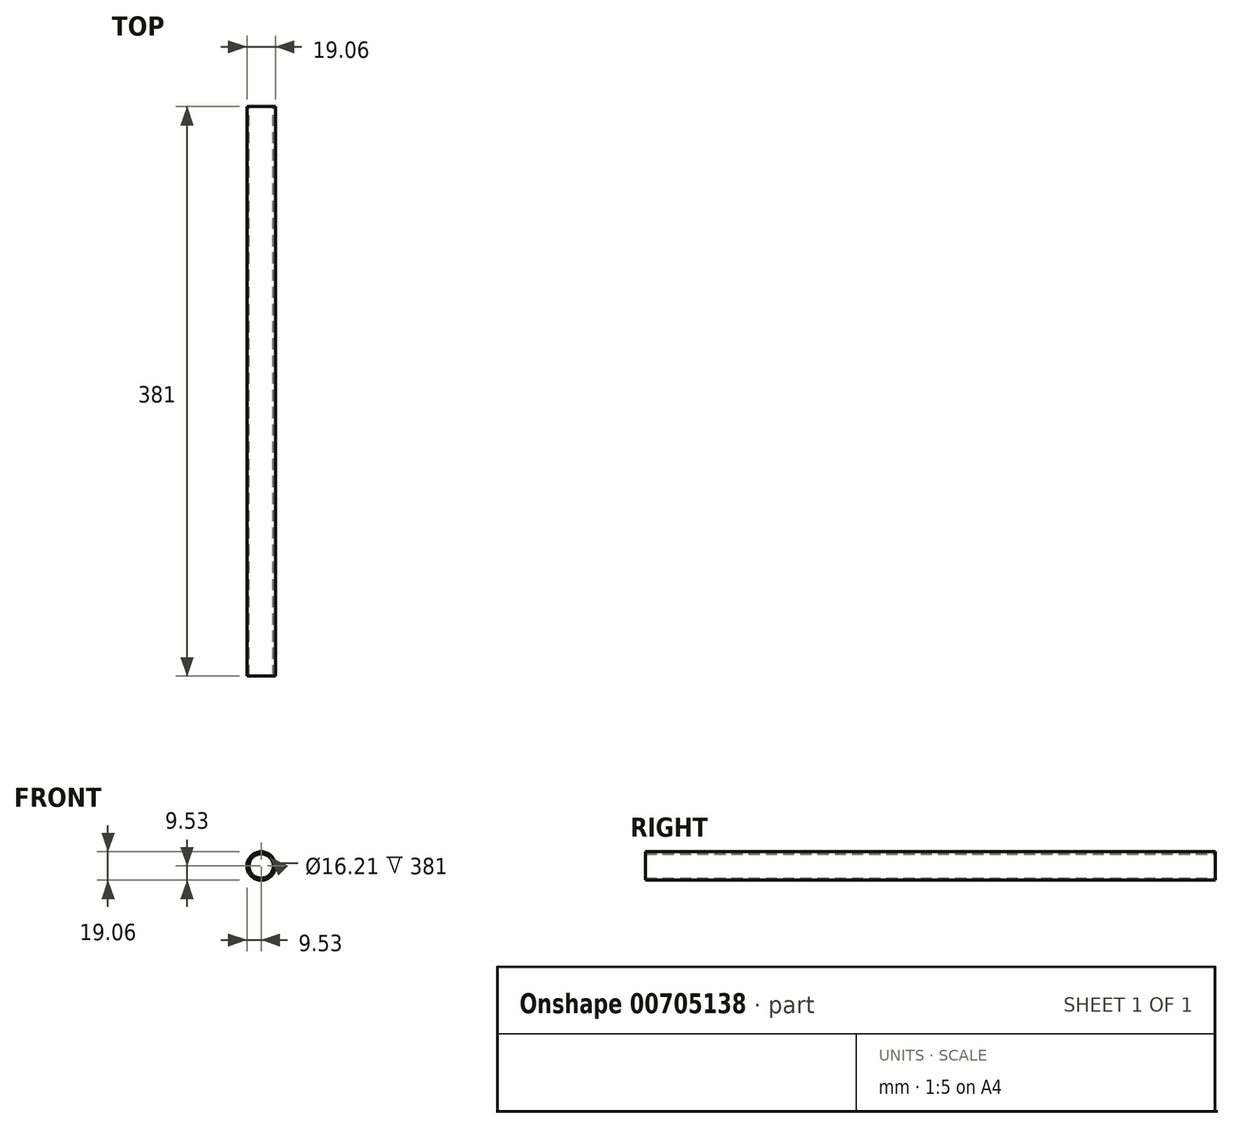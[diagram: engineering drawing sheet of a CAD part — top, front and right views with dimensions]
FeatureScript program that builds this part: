
annotation { "Feature Type Name" : "Feature", "Feature Type Description" : "" }
export const myFeature = defineFeature(function(context is Context, id is Id, definition is map)
    precondition{}
    {
        {
            var Q0;
            Q0=qCreatedBy(makeId("Front.planeOp"),FACE);
            var sketch = newSketch(context, id + "F0", { "sketchPlane" : qUnion([Q0])});
            skCircle(sketch, "E0", {"center": v(0, 0) * mm, "radius": 9.53 * mm});
            skCircle(sketch, "E1", {"center": v(0, 0) * mm, "radius": 8.1 * mm});
            skSolve(sketch);
        }
        {
            var Q0;
            Q0 = qSketchRegion(id + "F0", true);
            extrude(context, id + "F1", {"entities" : qUnion([Q0]), "depth" : 381 * mm, "offsetDistance" : 25.4 * mm});
        }
    });
